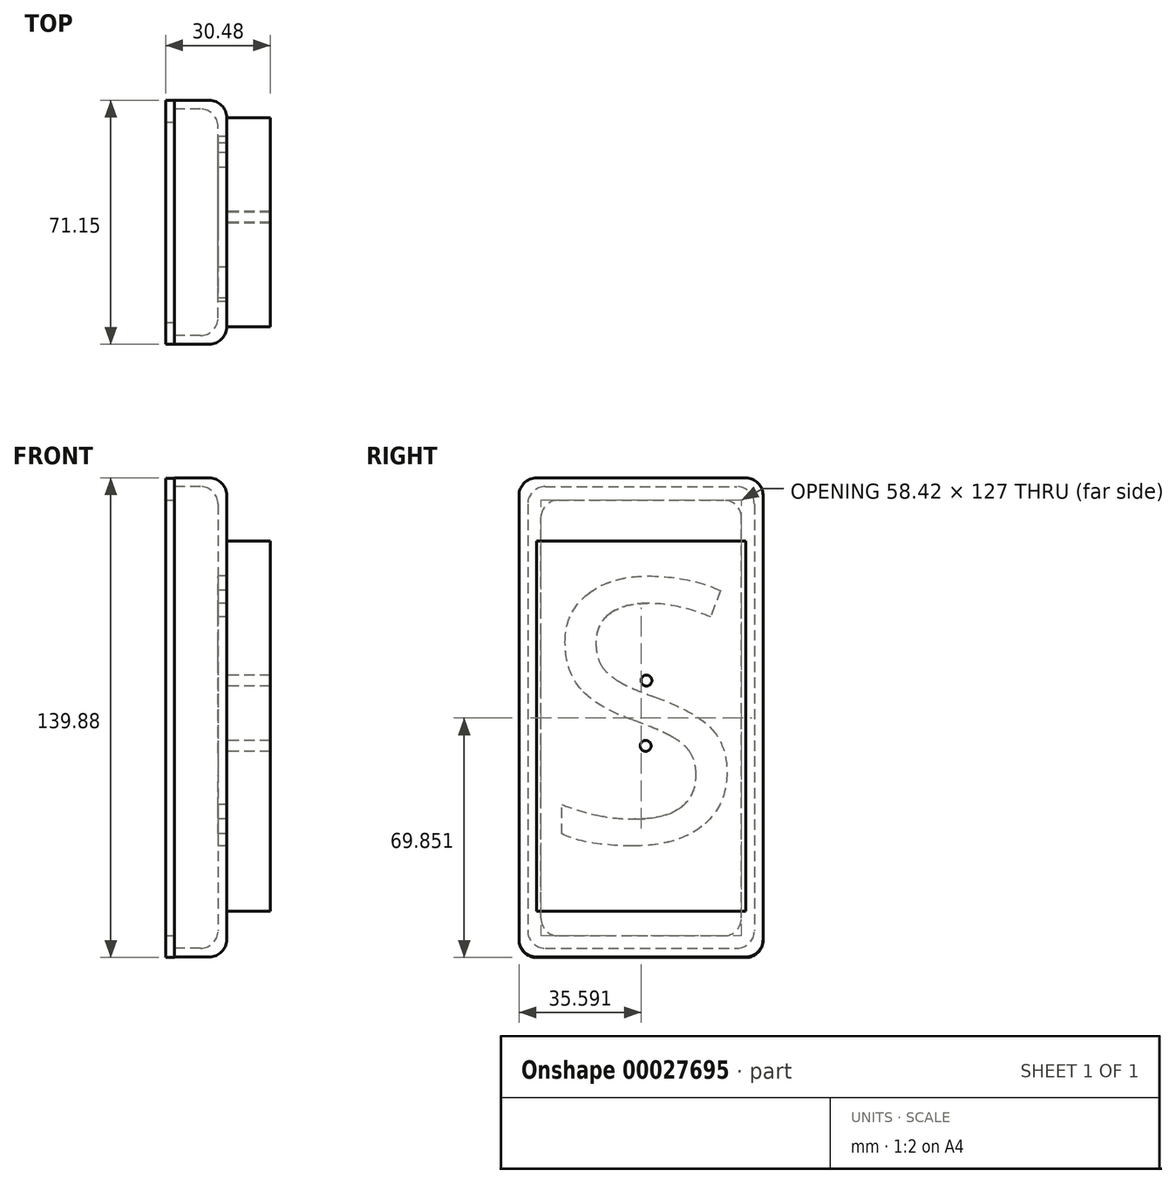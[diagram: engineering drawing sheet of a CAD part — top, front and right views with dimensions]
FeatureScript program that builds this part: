
annotation { "Feature Type Name" : "Feature", "Feature Type Description" : "" }
export const myFeature = defineFeature(function(context is Context, id is Id, definition is map)
    precondition{}
    {
        {
            var Q0;
            Q0=qCreatedBy(makeId("Right.planeOp"),FACE);
            var sketch = newSketch(context, id + "F0", { "sketchPlane" : qUnion([Q0])});
            skLineSegment(sketch, "E0.bottom", {"start": v(-41.84, 71.57) * mm, "end": v(29.28, 71.57) * mm});
            skLineSegment(sketch, "E0.top", {"start": v(-41.84, -68.13) * mm, "end": v(29.28, -68.13) * mm});
            skLineSegment(sketch, "E0.left", {"start": v(-41.84, 71.57) * mm, "end": v(-41.84, -68.13) * mm});
            skLineSegment(sketch, "E0.right", {"start": v(29.28, 71.57) * mm, "end": v(29.28, -68.13) * mm});
            skText(sketch, "E1", { "text": "S", "fontName": "OpenSans-Regular.ttf"});
            const initialGuessF0  = {"E1": [-0.03496, -0.03469, 1, 0, 0.0772]};
            skSetInitialGuess(sketch, initialGuessF0);
            skSolve(sketch);
        }
        {
            var Q0;
            Q0 = qSketchRegion(id + "F0", true);
            extrude(context, id + "F1", {"entities" : qUnion([Q0]), "depth" : 15.24 * mm});
        }
        {
            var Q0;
            Q0=makeQuery(id+"F1.opExtrude","SWEPT_FACE",FACE,{"disambiguationData":[OSD([sQuery(id+"F0.wireOp",EDGE,"E1.sketch_text.stroke-13")])]});
            var Q1;
            Q1=makeQuery(id+"F1.opExtrude","SWEPT_FACE",FACE,{"disambiguationData":[OSD([sQuery(id+"F0.wireOp",EDGE,"E1.sketch_text.stroke-12")])]});
            var Q2;
            Q2=makeQuery(id+"F1.opExtrude","SWEPT_FACE",FACE,{"disambiguationData":[OSD([sQuery(id+"F0.wireOp",EDGE,"E1.sketch_text.stroke-14")])]});
            var Q3;
            Q3=makeQuery(id+"F1.opExtrude","SWEPT_FACE",FACE,{"disambiguationData":[OSD([sQuery(id+"F0.wireOp",EDGE,"E1.sketch_text.stroke-15")])]});
            var Q4;
            Q4=makeQuery(id+"F1.opExtrude","SWEPT_FACE",FACE,{"disambiguationData":[OSD([sQuery(id+"F0.wireOp",EDGE,"E1.sketch_text.stroke-16")])]});
            var Q5;
            Q5=makeQuery(id+"F1.opExtrude","SWEPT_FACE",FACE,{"disambiguationData":[OSD([sQuery(id+"F0.wireOp",EDGE,"E1.sketch_text.stroke-17")])]});
            var Q6;
            Q6=makeQuery(id+"F1.opExtrude","SWEPT_FACE",FACE,{"disambiguationData":[OSD([sQuery(id+"F0.wireOp",EDGE,"E1.sketch_text.stroke-18")])]});
            var Q7;
            Q7=makeQuery(id+"F1.opExtrude","SWEPT_FACE",FACE,{"disambiguationData":[OSD([sQuery(id+"F0.wireOp",EDGE,"E1.sketch_text.stroke-19")])]});
            var Q8;
            Q8=makeQuery(id+"F1.opExtrude","SWEPT_FACE",FACE,{"disambiguationData":[OSD([sQuery(id+"F0.wireOp",EDGE,"E1.sketch_text.stroke-20")])]});
            var Q9;
            Q9=makeQuery(id+"F1.opExtrude","SWEPT_FACE",FACE,{"disambiguationData":[OSD([sQuery(id+"F0.wireOp",EDGE,"E1.sketch_text.stroke-21")])]});
            var Q10;
            Q10=makeQuery(id+"F1.opExtrude","SWEPT_FACE",FACE,{"disambiguationData":[OSD([sQuery(id+"F0.wireOp",EDGE,"E1.sketch_text.stroke-2")])]});
            var Q11;
            Q11=makeQuery(id+"F1.opExtrude","SWEPT_FACE",FACE,{"disambiguationData":[OSD([sQuery(id+"F0.wireOp",EDGE,"E1.sketch_text.stroke-1")])]});
            var Q12;
            Q12=makeQuery(id+"F1.opExtrude","SWEPT_FACE",FACE,{"disambiguationData":[OSD([sQuery(id+"F0.wireOp",EDGE,"E1.sketch_text.stroke-10")])]});
            var Q13;
            Q13=makeQuery(id+"F1.opExtrude","SWEPT_FACE",FACE,{"disambiguationData":[OSD([sQuery(id+"F0.wireOp",EDGE,"E1.sketch_text.stroke-8")])]});
            var Q14;
            Q14=makeQuery(id+"F1.opExtrude","SWEPT_FACE",FACE,{"disambiguationData":[OSD([sQuery(id+"F0.wireOp",EDGE,"E1.sketch_text.stroke-9")])]});
            var Q15;
            Q15=makeQuery(id+"F1.opExtrude","SWEPT_FACE",FACE,{"disambiguationData":[OSD([sQuery(id+"F0.wireOp",EDGE,"E1.sketch_text.stroke-11")])]});
            var Q16;
            Q16=makeQuery(id+"F1.opExtrude","SWEPT_FACE",FACE,{"disambiguationData":[OSD([sQuery(id+"F0.wireOp",EDGE,"E1.sketch_text.stroke-7")])]});
            var Q17;
            Q17=makeQuery(id+"F1.opExtrude","SWEPT_FACE",FACE,{"disambiguationData":[OSD([sQuery(id+"F0.wireOp",EDGE,"E1.sketch_text.stroke-6")])]});
            var Q18;
            Q18=makeQuery(id+"F1.opExtrude","SWEPT_FACE",FACE,{"disambiguationData":[OSD([sQuery(id+"F0.wireOp",EDGE,"E1.sketch_text.stroke-5")])]});
            var Q19;
            Q19=makeQuery(id+"F1.opExtrude","SWEPT_FACE",FACE,{"disambiguationData":[OSD([sQuery(id+"F0.wireOp",EDGE,"E1.sketch_text.stroke-4")])]});
            var Q20;
            Q20=makeQuery(id+"F1.opExtrude","SWEPT_FACE",FACE,{"disambiguationData":[OSD([sQuery(id+"F0.wireOp",EDGE,"E1.sketch_text.stroke-3")])]});
            var Q21;
            Q21=makeQuery(id+"F1.opExtrude","SWEPT_FACE",FACE,{"disambiguationData":[OSD([sQuery(id+"F0.wireOp",EDGE,"E1.sketch_text.stroke-0")])]});
            var Q22;
            Q22=makeQuery(id+"F1.opExtrude","SWEPT_FACE",FACE,{"disambiguationData":[OSD([sQuery(id+"F0.wireOp",EDGE,"E1.sketch_text.stroke-24")])]});
            var Q23;
            Q23=makeQuery(id+"F1.opExtrude","SWEPT_FACE",FACE,{"disambiguationData":[OSD([sQuery(id+"F0.wireOp",EDGE,"E1.sketch_text.stroke-22")])]});
            var Q24;
            Q24=makeQuery(id+"F1.opExtrude","CAP_FACE",FACE,{"disambiguationData":[OSD([sQuery(id+"F0.wireOp",EDGE,"E0.bottom"),sQuery(id+"F0.wireOp",EDGE,"E0.top"),sQuery(id+"F0.wireOp",EDGE,"E0.left"),sQuery(id+"F0.wireOp",EDGE,"E0.right"),sQuery(id+"F0.wireOp",EDGE,"E1.sketch_text.stroke-0"),sQuery(id+"F0.wireOp",EDGE,"E1.sketch_text.stroke-1"),sQuery(id+"F0.wireOp",EDGE,"E1.sketch_text.stroke-2"),sQuery(id+"F0.wireOp",EDGE,"E1.sketch_text.stroke-3"),sQuery(id+"F0.wireOp",EDGE,"E1.sketch_text.stroke-4"),sQuery(id+"F0.wireOp",EDGE,"E1.sketch_text.stroke-5"),sQuery(id+"F0.wireOp",EDGE,"E1.sketch_text.stroke-6"),sQuery(id+"F0.wireOp",EDGE,"E1.sketch_text.stroke-7"),sQuery(id+"F0.wireOp",EDGE,"E1.sketch_text.stroke-8"),sQuery(id+"F0.wireOp",EDGE,"E1.sketch_text.stroke-9"),sQuery(id+"F0.wireOp",EDGE,"E1.sketch_text.stroke-10"),sQuery(id+"F0.wireOp",EDGE,"E1.sketch_text.stroke-11"),sQuery(id+"F0.wireOp",EDGE,"E1.sketch_text.stroke-12"),sQuery(id+"F0.wireOp",EDGE,"E1.sketch_text.stroke-13"),sQuery(id+"F0.wireOp",EDGE,"E1.sketch_text.stroke-14"),sQuery(id+"F0.wireOp",EDGE,"E1.sketch_text.stroke-15"),sQuery(id+"F0.wireOp",EDGE,"E1.sketch_text.stroke-16"),sQuery(id+"F0.wireOp",EDGE,"E1.sketch_text.stroke-17"),sQuery(id+"F0.wireOp",EDGE,"E1.sketch_text.stroke-18"),sQuery(id+"F0.wireOp",EDGE,"E1.sketch_text.stroke-19"),sQuery(id+"F0.wireOp",EDGE,"E1.sketch_text.stroke-20"),sQuery(id+"F0.wireOp",EDGE,"E1.sketch_text.stroke-21"),sQuery(id+"F0.wireOp",EDGE,"E1.sketch_text.stroke-22"),sQuery(id+"F0.wireOp",EDGE,"E1.sketch_text.stroke-23"),sQuery(id+"F0.wireOp",EDGE,"E1.sketch_text.stroke-24")])],"isStart":true});
            var Q25;
            Q25=makeQuery(id+"F1.opExtrude","SWEPT_FACE",FACE,{"disambiguationData":[OSD([sQuery(id+"F0.wireOp",EDGE,"E1.sketch_text.stroke-23")])]});
            shell(context, id + "F2", {"entities" : qUnion([Q0, Q1, Q2, Q3, Q4, Q5, Q6, Q7, Q8, Q9, Q10, Q11, Q12, Q13, Q14, Q15, Q16, Q17, Q18, Q19, Q20, Q21, Q22, Q23, Q24, Q25]), "thickness" : 2.54 * mm});
        }
        {
            var Q0;
            Q0=makeQuery(id+"F1.opExtrude","CAP_EDGE",EDGE,{"disambiguationData":[OSD([sQuery(id+"F0.wireOp",EDGE,"E0.bottom")])],"isStart":false});
            var Q1;
            Q1=makeQuery(id+"F1.opExtrude","CAP_EDGE",EDGE,{"disambiguationData":[OSD([sQuery(id+"F0.wireOp",EDGE,"E0.left")])],"isStart":false});
            var Q2;
            Q2=makeQuery(id+"F1.opExtrude","CAP_EDGE",EDGE,{"disambiguationData":[OSD([sQuery(id+"F0.wireOp",EDGE,"E0.top")])],"isStart":false});
            var Q3;
            Q3=makeQuery(id+"F1.opExtrude","CAP_EDGE",EDGE,{"disambiguationData":[OSD([sQuery(id+"F0.wireOp",EDGE,"E0.right")])],"isStart":false});
            var Q4;
            {var subQ0=sQuery(id+"F0.wireOp",EDGE,"E0.top");Q4=makeQuery(id+"F2.opShell","OFFSET_EDGE",EDGE,{"disambiguationData":[OSD([subQ0]),TDD([makeQuery(id+"F1.opExtrude","CAP_EDGE",EDGE,{"disambiguationData":[OSD([subQ0])],"isStart":false})])]});}
            var Q5;
            {var subQ0=sQuery(id+"F0.wireOp",EDGE,"E0.left");Q5=makeQuery(id+"F2.opShell","OFFSET_EDGE",EDGE,{"disambiguationData":[OSD([subQ0]),TDD([makeQuery(id+"F1.opExtrude","CAP_EDGE",EDGE,{"disambiguationData":[OSD([subQ0])],"isStart":false})])]});}
            var Q6;
            {var subQ0=sQuery(id+"F0.wireOp",EDGE,"E0.right");Q6=makeQuery(id+"F2.opShell","OFFSET_EDGE",EDGE,{"disambiguationData":[OSD([subQ0]),TDD([makeQuery(id+"F1.opExtrude","CAP_EDGE",EDGE,{"disambiguationData":[OSD([subQ0])],"isStart":false})])]});}
            var Q7;
            {var subQ0=sQuery(id+"F0.wireOp",EDGE,"E0.bottom");Q7=makeQuery(id+"F2.opShell","OFFSET_EDGE",EDGE,{"disambiguationData":[OSD([subQ0]),TDD([makeQuery(id+"F1.opExtrude","CAP_EDGE",EDGE,{"disambiguationData":[OSD([subQ0])],"isStart":false})])]});}
            var Q8;
            Q8=makeQuery(id+"F1.opExtrude","SWEPT_EDGE",EDGE,{"disambiguationData":[OSD([sQuery(id+"F0.wireOp",EDGE,"E0.bottom"),sQuery(id+"F0.wireOp",EDGE,"E0.right")])]});
            var Q9;
            Q9=makeQuery(id+"F1.opExtrude","SWEPT_EDGE",EDGE,{"disambiguationData":[OSD([sQuery(id+"F0.wireOp",EDGE,"E0.bottom"),sQuery(id+"F0.wireOp",EDGE,"E0.left")])]});
            var Q10;
            Q10=makeQuery(id+"F1.opExtrude","SWEPT_EDGE",EDGE,{"disambiguationData":[OSD([sQuery(id+"F0.wireOp",EDGE,"E0.top"),sQuery(id+"F0.wireOp",EDGE,"E0.left")])]});
            var Q11;
            Q11=makeQuery(id+"F1.opExtrude","SWEPT_EDGE",EDGE,{"disambiguationData":[OSD([sQuery(id+"F0.wireOp",EDGE,"E0.top"),sQuery(id+"F0.wireOp",EDGE,"E0.right")])]});
            var Q12;
            Q12=makeQuery(id+"F2.opShell","OFFSET_EDGE",EDGE,{"disambiguationData":[OSD([sQuery(id+"F0.wireOp",EDGE,"E0.top"),sQuery(id+"F0.wireOp",EDGE,"E0.left")])]});
            var Q13;
            Q13=makeQuery(id+"F2.opShell","OFFSET_EDGE",EDGE,{"disambiguationData":[OSD([sQuery(id+"F0.wireOp",EDGE,"E0.bottom"),sQuery(id+"F0.wireOp",EDGE,"E0.left")])]});
            var Q14;
            Q14=makeQuery(id+"F2.opShell","OFFSET_EDGE",EDGE,{"disambiguationData":[OSD([sQuery(id+"F0.wireOp",EDGE,"E0.top"),sQuery(id+"F0.wireOp",EDGE,"E0.right")])]});
            var Q15;
            Q15=makeQuery(id+"F2.opShell","OFFSET_EDGE",EDGE,{"disambiguationData":[OSD([sQuery(id+"F0.wireOp",EDGE,"E0.bottom"),sQuery(id+"F0.wireOp",EDGE,"E0.right")])]});
            fillet(context, id + "F3", {"entities" : qUnion([Q0, Q1, Q2, Q3, Q4, Q5, Q6, Q7, Q8, Q9, Q10, Q11, Q12, Q13, Q14, Q15]), "radius" : 5.08 * mm, "tangentPropagation" : true, "allowEdgeOverflow" : false});
        }
        {
            var Q0;
            Q0=makeQuery(id+"F1.opExtrude","CAP_FACE",FACE,{"disambiguationData":[OSD([sQuery(id+"F0.wireOp",EDGE,"E0.bottom"),sQuery(id+"F0.wireOp",EDGE,"E0.top"),sQuery(id+"F0.wireOp",EDGE,"E0.left"),sQuery(id+"F0.wireOp",EDGE,"E0.right"),sQuery(id+"F0.wireOp",EDGE,"E1.sketch_text.stroke-0"),sQuery(id+"F0.wireOp",EDGE,"E1.sketch_text.stroke-1"),sQuery(id+"F0.wireOp",EDGE,"E1.sketch_text.stroke-2"),sQuery(id+"F0.wireOp",EDGE,"E1.sketch_text.stroke-3"),sQuery(id+"F0.wireOp",EDGE,"E1.sketch_text.stroke-4"),sQuery(id+"F0.wireOp",EDGE,"E1.sketch_text.stroke-5"),sQuery(id+"F0.wireOp",EDGE,"E1.sketch_text.stroke-6"),sQuery(id+"F0.wireOp",EDGE,"E1.sketch_text.stroke-7"),sQuery(id+"F0.wireOp",EDGE,"E1.sketch_text.stroke-8"),sQuery(id+"F0.wireOp",EDGE,"E1.sketch_text.stroke-9"),sQuery(id+"F0.wireOp",EDGE,"E1.sketch_text.stroke-10"),sQuery(id+"F0.wireOp",EDGE,"E1.sketch_text.stroke-11"),sQuery(id+"F0.wireOp",EDGE,"E1.sketch_text.stroke-12"),sQuery(id+"F0.wireOp",EDGE,"E1.sketch_text.stroke-13"),sQuery(id+"F0.wireOp",EDGE,"E1.sketch_text.stroke-14"),sQuery(id+"F0.wireOp",EDGE,"E1.sketch_text.stroke-15"),sQuery(id+"F0.wireOp",EDGE,"E1.sketch_text.stroke-16"),sQuery(id+"F0.wireOp",EDGE,"E1.sketch_text.stroke-17"),sQuery(id+"F0.wireOp",EDGE,"E1.sketch_text.stroke-18"),sQuery(id+"F0.wireOp",EDGE,"E1.sketch_text.stroke-19"),sQuery(id+"F0.wireOp",EDGE,"E1.sketch_text.stroke-20"),sQuery(id+"F0.wireOp",EDGE,"E1.sketch_text.stroke-21"),sQuery(id+"F0.wireOp",EDGE,"E1.sketch_text.stroke-22"),sQuery(id+"F0.wireOp",EDGE,"E1.sketch_text.stroke-23"),sQuery(id+"F0.wireOp",EDGE,"E1.sketch_text.stroke-24")])],"isStart":false});
            var sketch = newSketch(context, id + "F4", { "sketchPlane" : qUnion([Q0])});
            skLineSegment(sketch, "E2.bottom", {"start": v(-36.76, 53.17) * mm, "end": v(24.2, 53.17) * mm});
            skLineSegment(sketch, "E2.top", {"start": v(-36.76, -54.81) * mm, "end": v(24.2, -54.81) * mm});
            skLineSegment(sketch, "E2.left", {"start": v(-36.76, 53.17) * mm, "end": v(-36.76, -54.81) * mm});
            skLineSegment(sketch, "E2.right", {"start": v(24.2, 53.17) * mm, "end": v(24.2, -54.81) * mm});
            skCircle(sketch, "E3", {"center": v(-4.7, 12.46) * mm, "radius": 1.59 * mm});
            skCircle(sketch, "E4", {"center": v(-4.93, -6.59) * mm, "radius": 1.59 * mm});
            skSolve(sketch);
        }
        {
            var Q0;
            Q0 = qSketchRegion(id + "F4", true);
            extrude(context, id + "F5", {"entities" : qUnion([Q0]), "operationType" : NewBodyOperationType.ADD, "depth" : 12.7 * mm});
        }
        {
            var Q0;
            Q0=makeQuery(id+"F1.opExtrude","CAP_FACE",FACE,{"disambiguationData":[OSD([sQuery(id+"F0.wireOp",EDGE,"E0.bottom"),sQuery(id+"F0.wireOp",EDGE,"E0.top"),sQuery(id+"F0.wireOp",EDGE,"E0.left"),sQuery(id+"F0.wireOp",EDGE,"E0.right"),sQuery(id+"F0.wireOp",EDGE,"E1.sketch_text.stroke-0"),sQuery(id+"F0.wireOp",EDGE,"E1.sketch_text.stroke-1"),sQuery(id+"F0.wireOp",EDGE,"E1.sketch_text.stroke-2"),sQuery(id+"F0.wireOp",EDGE,"E1.sketch_text.stroke-3"),sQuery(id+"F0.wireOp",EDGE,"E1.sketch_text.stroke-4"),sQuery(id+"F0.wireOp",EDGE,"E1.sketch_text.stroke-5"),sQuery(id+"F0.wireOp",EDGE,"E1.sketch_text.stroke-6"),sQuery(id+"F0.wireOp",EDGE,"E1.sketch_text.stroke-7"),sQuery(id+"F0.wireOp",EDGE,"E1.sketch_text.stroke-8"),sQuery(id+"F0.wireOp",EDGE,"E1.sketch_text.stroke-9"),sQuery(id+"F0.wireOp",EDGE,"E1.sketch_text.stroke-10"),sQuery(id+"F0.wireOp",EDGE,"E1.sketch_text.stroke-11"),sQuery(id+"F0.wireOp",EDGE,"E1.sketch_text.stroke-12"),sQuery(id+"F0.wireOp",EDGE,"E1.sketch_text.stroke-13"),sQuery(id+"F0.wireOp",EDGE,"E1.sketch_text.stroke-14"),sQuery(id+"F0.wireOp",EDGE,"E1.sketch_text.stroke-15"),sQuery(id+"F0.wireOp",EDGE,"E1.sketch_text.stroke-16"),sQuery(id+"F0.wireOp",EDGE,"E1.sketch_text.stroke-17"),sQuery(id+"F0.wireOp",EDGE,"E1.sketch_text.stroke-18"),sQuery(id+"F0.wireOp",EDGE,"E1.sketch_text.stroke-19"),sQuery(id+"F0.wireOp",EDGE,"E1.sketch_text.stroke-20"),sQuery(id+"F0.wireOp",EDGE,"E1.sketch_text.stroke-21"),sQuery(id+"F0.wireOp",EDGE,"E1.sketch_text.stroke-22"),sQuery(id+"F0.wireOp",EDGE,"E1.sketch_text.stroke-23"),sQuery(id+"F0.wireOp",EDGE,"E1.sketch_text.stroke-24")])],"isStart":true});
            var sketch = newSketch(context, id + "F6", { "sketchPlane" : qUnion([Q0])});
            skLineSegment(sketch, "E5.bottom", {"start": v(-29.31, 71.4) * mm, "end": v(41.8, 71.4) * mm});
            skLineSegment(sketch, "E5.top", {"start": v(-29.31, -68.3) * mm, "end": v(41.8, -68.3) * mm});
            skLineSegment(sketch, "E5.left", {"start": v(-29.31, 71.4) * mm, "end": v(-29.31, -68.3) * mm});
            skLineSegment(sketch, "E5.right", {"start": v(41.8, 71.4) * mm, "end": v(41.8, -68.3) * mm});
            skLineSegment(sketch, "E6.bottom", {"start": v(35.46, -61.96) * mm, "end": v(-22.96, -61.96) * mm});
            skLineSegment(sketch, "E6.top", {"start": v(35.46, 65.04) * mm, "end": v(-22.96, 65.04) * mm});
            skLineSegment(sketch, "E6.left", {"start": v(35.46, -61.96) * mm, "end": v(35.46, 65.04) * mm});
            skLineSegment(sketch, "E6.right", {"start": v(-22.96, -61.96) * mm, "end": v(-22.96, 65.04) * mm});
            skSolve(sketch);
        }
        {
            var Q0;
            Q0 = qSketchRegion(id + "F6", true);
            extrude(context, id + "F7", {"entities" : qUnion([Q0]), "operationType" : NewBodyOperationType.ADD, "depth" : 2.54 * mm});
        }
        {
            var Q0;
            Q0=makeQuery(id+"F7.opExtrude","SWEPT_EDGE",EDGE,{"disambiguationData":[OSD([sQuery(id+"F6.wireOp",EDGE,"E5.bottom"),sQuery(id+"F6.wireOp",EDGE,"E5.left")])]});
            var Q1;
            Q1=makeQuery(id+"F7.opExtrude","SWEPT_EDGE",EDGE,{"disambiguationData":[OSD([sQuery(id+"F6.wireOp",EDGE,"E5.bottom"),sQuery(id+"F6.wireOp",EDGE,"E5.right")])]});
            var Q2;
            Q2=makeQuery(id+"F7.opExtrude","SWEPT_EDGE",EDGE,{"disambiguationData":[OSD([sQuery(id+"F6.wireOp",EDGE,"E5.top"),sQuery(id+"F6.wireOp",EDGE,"E5.right")])]});
            var Q3;
            Q3=makeQuery(id+"F7.opExtrude","SWEPT_EDGE",EDGE,{"disambiguationData":[OSD([sQuery(id+"F6.wireOp",EDGE,"E5.top"),sQuery(id+"F6.wireOp",EDGE,"E5.left")])]});
            var Q4;
            Q4=makeQuery(id+"F7.opExtrude","SWEPT_EDGE",EDGE,{"disambiguationData":[OSD([sQuery(id+"F6.wireOp",EDGE,"E6.top"),sQuery(id+"F6.wireOp",EDGE,"E6.right")])]});
            var Q5;
            Q5=makeQuery(id+"F7.opExtrude","SWEPT_EDGE",EDGE,{"disambiguationData":[OSD([sQuery(id+"F6.wireOp",EDGE,"E6.bottom"),sQuery(id+"F6.wireOp",EDGE,"E6.right")])]});
            var Q6;
            Q6=makeQuery(id+"F7.opExtrude","SWEPT_EDGE",EDGE,{"disambiguationData":[OSD([sQuery(id+"F6.wireOp",EDGE,"E6.bottom"),sQuery(id+"F6.wireOp",EDGE,"E6.left")])]});
            var Q7;
            Q7=makeQuery(id+"F7.opExtrude","SWEPT_EDGE",EDGE,{"disambiguationData":[OSD([sQuery(id+"F6.wireOp",EDGE,"E6.top"),sQuery(id+"F6.wireOp",EDGE,"E6.left")])]});
            fillet(context, id + "F8", {"entities" : qUnion([Q0, Q1, Q2, Q3, Q4, Q5, Q6, Q7]), "radius" : 5.08 * mm, "tangentPropagation" : true, "allowEdgeOverflow" : false});
        }
    });
